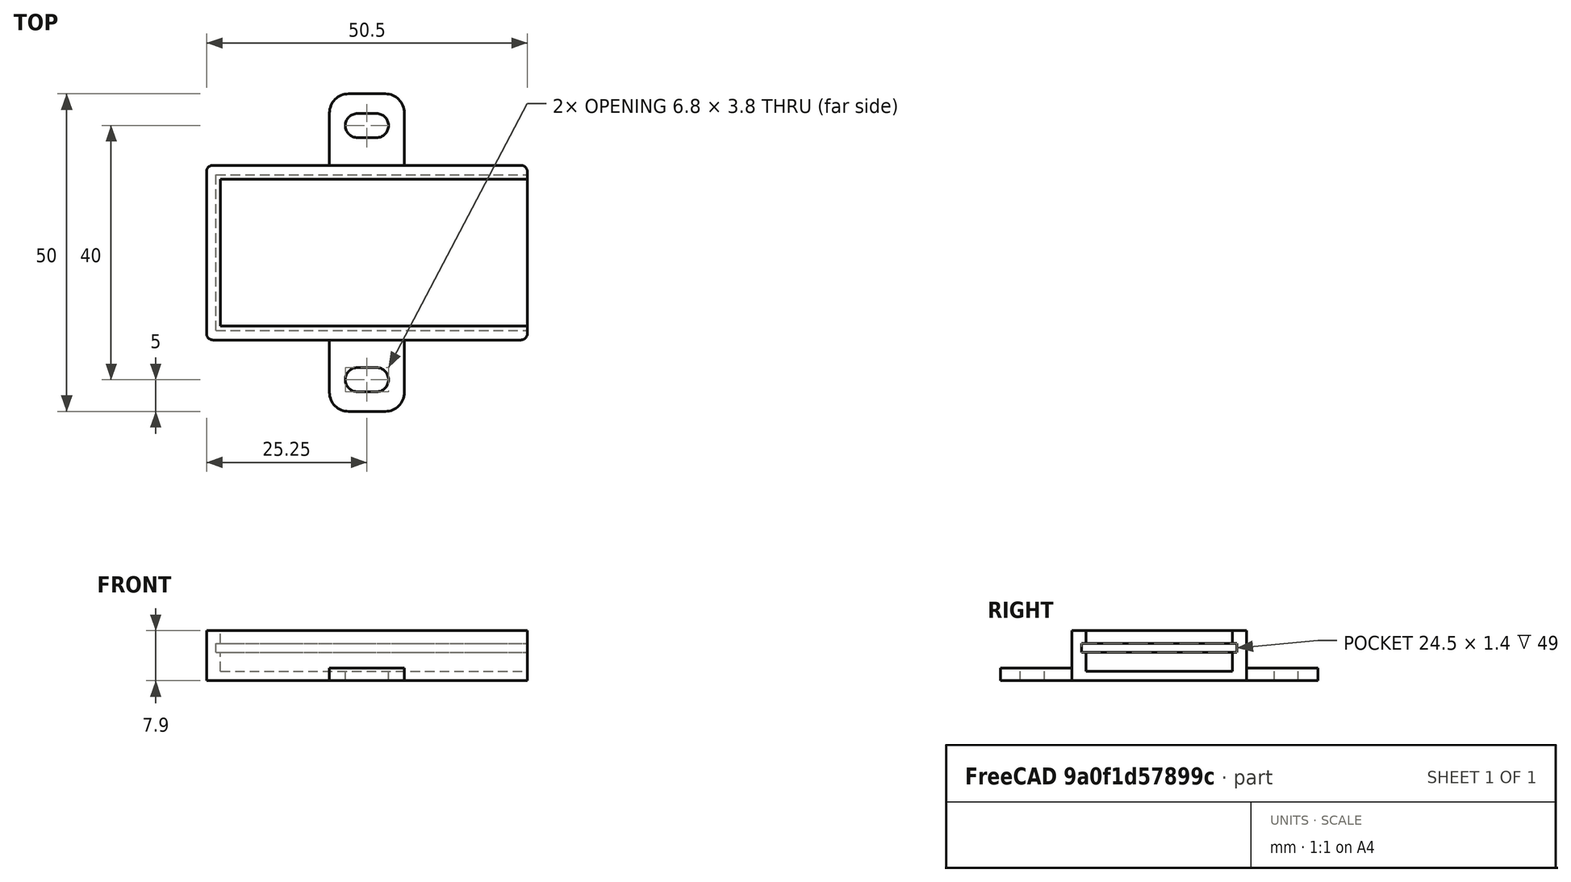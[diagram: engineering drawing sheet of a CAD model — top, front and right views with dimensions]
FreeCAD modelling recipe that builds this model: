
FCSTD DOCUMENT  (FreeCAD 0.19R23578 (Git))
Label: step_down_lm2596s
License: FreeArt
LicenseURL: http://artlibre.org/licence/lal
objects: Part::Box×3, Part::MultiFuse×2, Spreadsheet::Sheet×1, Part::Fillet×1, Part::Feature×1, Part::Cut×1, App::Part×1
note: 8 computed .brp shape members not serialized (recipe doc carries the construction recipe); baked Part::Feature solids carry a one-line shape summary decoded from their .brp

FEATURE [Spreadsheet::Sheet] Spreadsheet  label="p"
  cells = A1=pcb_x; B1(pcb_x)=49; A2=pcb_y; B2(pcb_y)=24.5; A3=pcb_z; B3(pcb_z)=1.4; A4=pcb_under; B4(pcb_under)=3; A5=side_wall; B5(side_wall)=1.5; A6=pcb_side_lane; B6(pcb_side_lane)=0.7; A7=bottom_wall; B7(bottom_wall)=1.5; A8=pcb_above; B8(pcb_above)=2
FEATURE [Part::Box] Box  label="external cube"
  AttacherType = Attacher::AttachEngine3D
  Height = 7.9
  Length = 50.5
  Width = 27.5
  expr: Length = <<p>>.pcb_x + <<p>>.side_wall
  expr: Width = <<p>>.pcb_y + 2 * <<p>>.side_wall
  expr: Height = <<p>>.bottom_wall + <<p>>.pcb_under + <<p>>.pcb_z + <<p>>.pcb_above
FEATURE [Part::Box] Box006  label="internal cube"
  AttacherType = Attacher::AttachEngine3D
  Height = 6.4
  Length = 49.1
  Placement = pos=(2.2,2.2,1.5) rot=(0,0,1;0rad)
  Width = 23.1
  expr: Length = <<p>>.pcb_x - 2 * <<p>>.pcb_side_lane + <<p>>.side_wall
  expr: Width = <<p>>.pcb_y - 2 * <<p>>.pcb_side_lane
  expr: Height = <<p>>.pcb_under + <<p>>.pcb_z + <<p>>.pcb_above
  expr: .Placement.Base.z = <<p>>.bottom_wall
  expr: .Placement.Base.x = <<p>>.side_wall + <<p>>.pcb_side_lane
  expr: .Placement.Base.y = <<p>>.side_wall + <<p>>.pcb_side_lane
FEATURE [Part::Box] Box007  label="pcb extract cube"
  AttacherType = Attacher::AttachEngine3D
  Height = 1.4
  Length = 49
  Placement = pos=(1.5,1.5,4.5) rot=(0,0,1;0rad)
  Width = 24.5
  expr: Height = <<p>>.pcb_z
  expr: .Placement.Base.z = <<p>>.bottom_wall + <<p>>.pcb_under
  expr: Width = <<p>>.pcb_y
  expr: Length = <<p>>.pcb_x
  expr: .Placement.Base.x = <<p>>.side_wall
  expr: .Placement.Base.y = <<p>>.side_wall
FEATURE [Part::MultiFuse] Fusion  label="extract fusion"
  Shapes = -> [Box006,Box007]
FEATURE [Part::Fillet] Fillet  label="external fillet"
  Base = -> Box
  Edges = 4 edges r=1: [Edge1,Edge3,Edge5,Edge7]
FEATURE [Part::Feature] Cut002001  label="attach plane y dir001"
  Placement = pos=(19.35,-11.25,0) rot=(0,0,1;0rad)
  shape: bbox 11.8 x 50 x 2 mm, 20 faces (baked)
FEATURE [Part::MultiFuse] Fusion001  label="solid fusion"
  Shapes = -> [Fillet,Cut002001]
FEATURE [Part::Cut] Cut  label="body cut"
  Base = -> Fusion001
  Tool = -> Fusion
FEATURE [App::Part] Part  label="lm2596s pcb box part"
  Group = -> [Box,Fillet,Fusion001,Fusion,Box007,Box006,Cut]
  Origin = -> Origin
